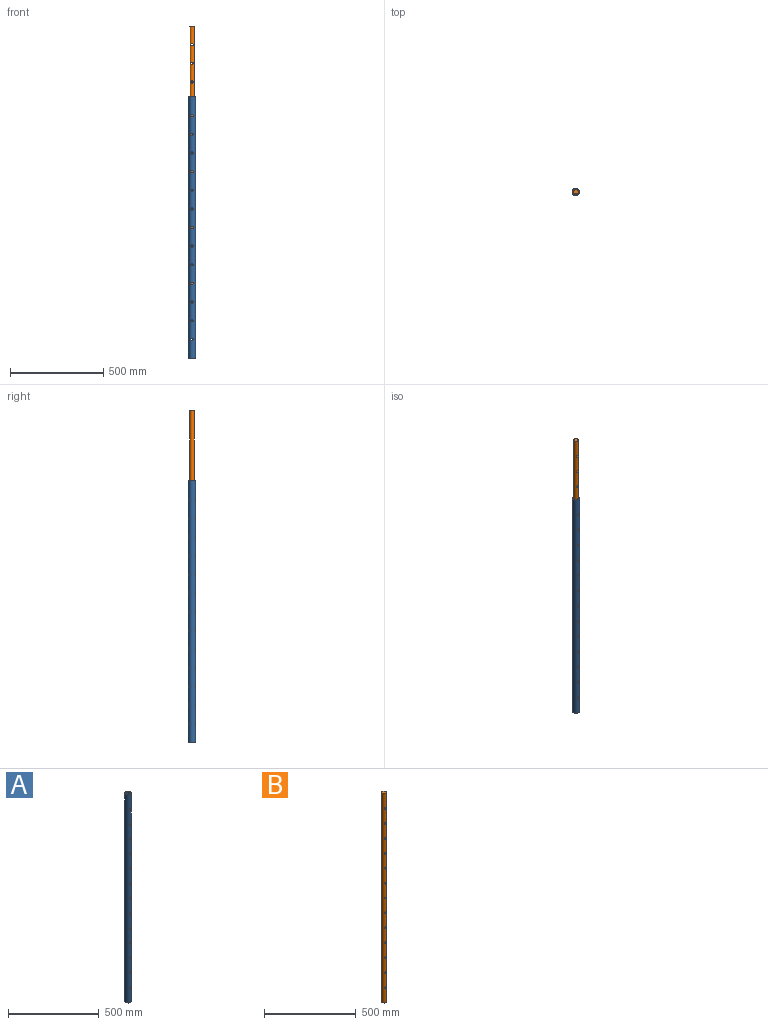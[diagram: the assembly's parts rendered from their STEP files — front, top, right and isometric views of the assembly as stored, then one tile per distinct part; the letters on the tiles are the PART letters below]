
ASSEMBLY  parts=2 mates=1
PART A: 30 faces, bbox 38.1x38.1x1400 mm
  f0: cylinder r=12.7mm len=1400mm, axis (0,0,-1), area 108304.9mm2, adj f2,f3,f4,f5,f6,f7,f8,f9
  f1: cylinder r=19.05mm len=1400mm, axis (0,0,-1), area 164234.9mm2, adj f2,f3,f4,f5,f6,f7,f8,f9
  f2: plane 38.1x38.1mm, normal (0,0,1), area 633.4mm2, adj f0,f1
  f3: plane 38.1x38.1mm, normal (0,0,-1), area 633.4mm2, adj f0,f1
  f4: cylinder r=6.35mm len=12.7mm, axis (0,-1,0), area 265.1mm2, adj f0,f1
  f5: cylinder r=6.35mm len=12.7mm, axis (0,-1,0), area 265.1mm2, adj f0,f1
  f6: cylinder r=6.35mm len=12.7mm, axis (0,-1,0), area 265.1mm2, adj f0,f1
  f7: cylinder r=6.35mm len=12.7mm, axis (0,-1,0), area 265.1mm2, adj f0,f1
  f8: cylinder r=6.35mm len=12.7mm, axis (0,-1,0), area 265.1mm2, adj f0,f1
  f9: cylinder r=6.35mm len=12.7mm, axis (0,-1,0), area 265.1mm2, adj f0,f1
  f10: cylinder r=6.35mm len=12.7mm, axis (0,-1,0), area 265.1mm2, adj f0,f1
  f11: cylinder r=6.35mm len=12.7mm, axis (0,-1,0), area 265.1mm2, adj f0,f1
  f12: cylinder r=6.35mm len=12.7mm, axis (0,-1,0), area 265.1mm2, adj f0,f1
  f13: cylinder r=6.35mm len=12.7mm, axis (0,-1,0), area 265.1mm2, adj f0,f1
  f14: cylinder r=6.35mm len=12.7mm, axis (0,-1,0), area 265.1mm2, adj f0,f1
  f15: cylinder r=6.35mm len=12.7mm, axis (0,-1,0), area 265.1mm2, adj f0,f1
  f16: cylinder r=6.35mm len=12.7mm, axis (0,-1,0), area 265.1mm2, adj f0,f1
  f17: cylinder r=6.35mm len=12.7mm, axis (0,-1,0), area 265.1mm2, adj f0,f1
  f18: cylinder r=6.35mm len=12.7mm, axis (0,-1,0), area 265.1mm2, adj f0,f1
  f19: cylinder r=6.35mm len=12.7mm, axis (0,-1,0), area 265.1mm2, adj f0,f1
  f20: cylinder r=6.35mm len=12.7mm, axis (0,-1,0), area 265.1mm2, adj f0,f1
  f21: cylinder r=6.35mm len=12.7mm, axis (0,-1,0), area 265.1mm2, adj f0,f1
  f22: cylinder r=6.35mm len=12.7mm, axis (0,-1,0), area 265.1mm2, adj f0,f1
  f23: cylinder r=6.35mm len=12.7mm, axis (0,-1,0), area 265.1mm2, adj f0,f1
  f24: cylinder r=6.35mm len=12.7mm, axis (0,-1,0), area 265.1mm2, adj f0,f1
  f25: cylinder r=6.35mm len=12.7mm, axis (0,-1,0), area 265.1mm2, adj f0,f1
  f26: cylinder r=6.35mm len=12.7mm, axis (0,-1,0), area 265.1mm2, adj f0,f1
  f27: cylinder r=6.35mm len=12.7mm, axis (0,-1,0), area 265.1mm2, adj f0,f1
  f28: cylinder r=6.35mm len=12.7mm, axis (0,-1,0), area 265.1mm2, adj f0,f1
  f29: cylinder r=6.35mm len=12.7mm, axis (0,-1,0), area 265.1mm2, adj f0,f1
PART B: 16 faces, bbox 25.4x25.4x1400 mm
  f0: cylinder r=12.7mm len=1400mm, axis (0,0,-1), area 108304.9mm2, adj f1,f2,f3,f4,f5,f6,f7,f8
  f1: plane 25.4x25.4mm, normal (0,0,1), area 506.7mm2, adj f0
  f2: plane 25.4x25.4mm, normal (0,0,-1), area 506.7mm2, adj f0
  f3: cylinder r=6.35mm len=25.4mm, axis (0,-1,0), area 946.7mm2, adj f0
  f4: cylinder r=6.35mm len=25.4mm, axis (0,-1,0), area 946.7mm2, adj f0
  f5: cylinder r=6.35mm len=25.4mm, axis (0,-1,0), area 946.7mm2, adj f0
  f6: cylinder r=6.35mm len=25.4mm, axis (0,-1,0), area 946.7mm2, adj f0
  f7: cylinder r=6.35mm len=25.4mm, axis (0,-1,0), area 946.7mm2, adj f0
  f8: cylinder r=6.35mm len=25.4mm, axis (0,-1,0), area 946.7mm2, adj f0
  f9: cylinder r=6.35mm len=25.4mm, axis (0,-1,0), area 946.7mm2, adj f0
  f10: cylinder r=6.35mm len=25.4mm, axis (0,-1,0), area 946.7mm2, adj f0
  f11: cylinder r=6.35mm len=25.4mm, axis (0,-1,0), area 946.7mm2, adj f0
  f12: cylinder r=6.35mm len=25.4mm, axis (0,-1,0), area 946.7mm2, adj f0
  f13: cylinder r=6.35mm len=25.4mm, axis (0,-1,0), area 946.7mm2, adj f0
  f14: cylinder r=6.35mm len=25.4mm, axis (0,-1,0), area 946.7mm2, adj f0
  f15: cylinder r=6.35mm len=25.4mm, axis (0,-1,0), area 946.7mm2, adj f0
PLACE A t=(-601.56,256.96,295.6)mm fixed
PLACE B t=(-601.56,256.96,676.19)mm
MATE slider A.f1 <-> B.f0  axis (0,0,-1) through (-601.56,256.96,1695.6)mm
